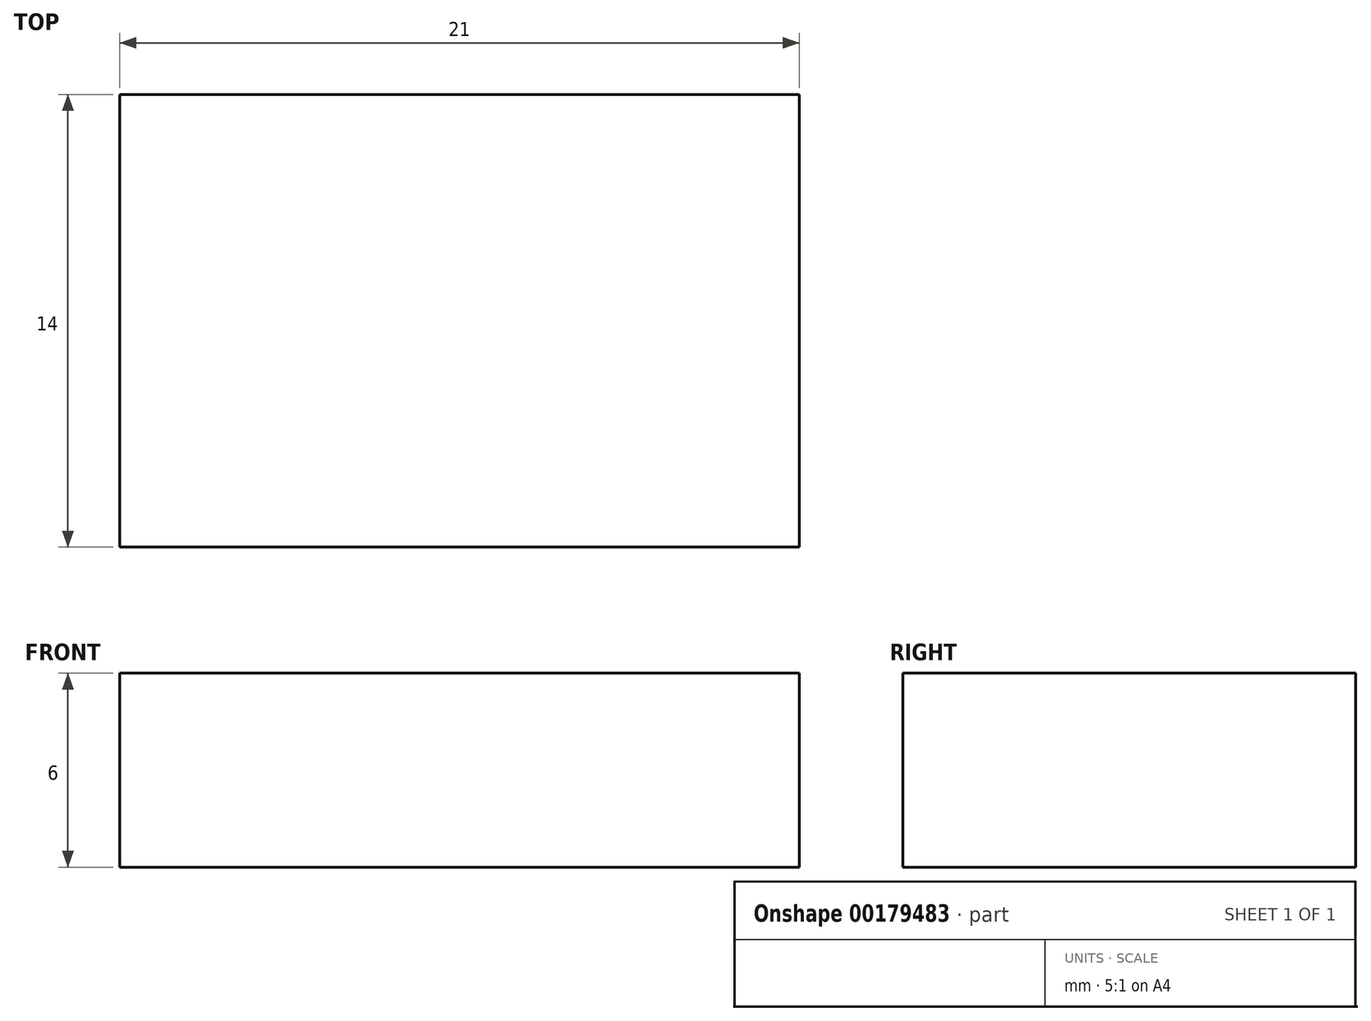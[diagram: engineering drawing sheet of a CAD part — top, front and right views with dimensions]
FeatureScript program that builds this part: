
annotation { "Feature Type Name" : "Feature", "Feature Type Description" : "" }
export const myFeature = defineFeature(function(context is Context, id is Id, definition is map)
    precondition{}
    {
        {
            var Q0;
            Q0=qCreatedBy(makeId("Top.planeOp"),FACE);
            var sketch = newSketch(context, id + "F0", { "sketchPlane" : qUnion([Q0])});
            skLineSegment(sketch, "E0.bottom", {"start": v(10.5, 7) * mm, "end": v(-10.5, 7) * mm});
            skLineSegment(sketch, "E0.top", {"start": v(10.5, -7) * mm, "end": v(-10.5, -7) * mm});
            skLineSegment(sketch, "E0.left", {"start": v(10.5, 7) * mm, "end": v(10.5, -7) * mm});
            skLineSegment(sketch, "E0.right", {"start": v(-10.5, 7) * mm, "end": v(-10.5, -7) * mm});
            skPoint(sketch, "E0.middle", {"position": v(0, 0) * mm});
            skSolve(sketch);
        }
        {
            var Q0;
            Q0 = qSketchRegion(id + "F0", true);
            extrude(context, id + "F1", {"entities" : qUnion([Q0]), "depth" : 6 * mm});
        }
    });
